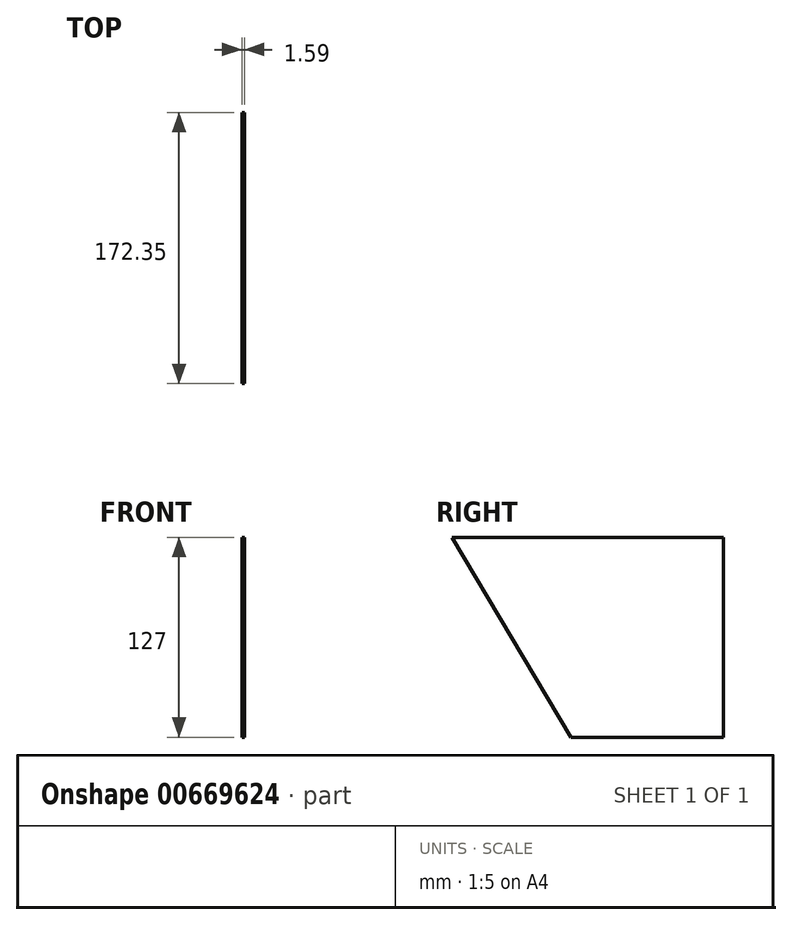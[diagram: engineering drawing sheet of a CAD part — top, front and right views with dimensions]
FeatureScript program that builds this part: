
annotation { "Feature Type Name" : "Feature", "Feature Type Description" : "" }
export const myFeature = defineFeature(function(context is Context, id is Id, definition is map)
    precondition{}
    {
        {
            var Q0;
            Q0=qCreatedBy(makeId("Right.planeOp"),FACE);
            var sketch = newSketch(context, id + "F0", { "sketchPlane" : qUnion([Q0])});
            skLineSegment(sketch, "E0", {"start": v(-98.12, 145.74) * mm, "end": v(74.23, 145.74) * mm});
            skLineSegment(sketch, "E1", {"start": v(74.23, 145.74) * mm, "end": v(74.23, 18.74) * mm});
            skLineSegment(sketch, "E2", {"start": v(74.23, 18.74) * mm, "end": v(-22.54, 18.74) * mm});
            skLineSegment(sketch, "E3", {"start": v(-22.54, 18.74) * mm, "end": v(-98.12, 145.74) * mm});
            skSolve(sketch);
        }
        {
            var Q0;
            Q0=qSketchRegion(id+"F0",true);
            extrude(context, id + "F1", {"entities" : qUnion([Q0]), "depth" : 1.59 * mm, "offsetDistance" : 25.4 * mm});
        }
    });
